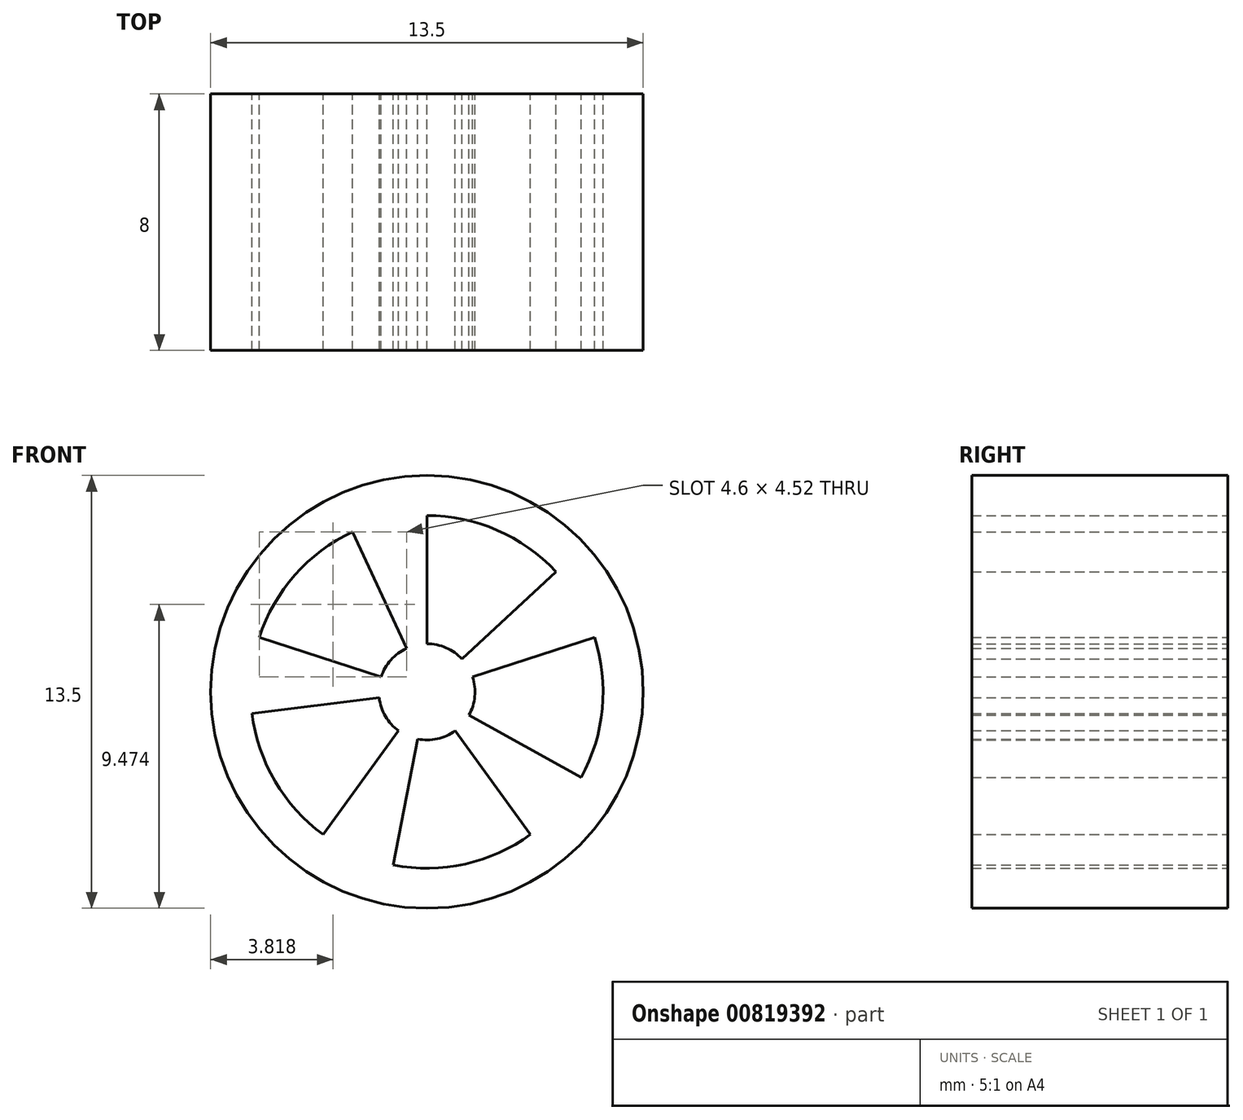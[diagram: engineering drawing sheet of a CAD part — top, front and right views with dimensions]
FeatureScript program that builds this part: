
annotation { "Feature Type Name" : "Feature", "Feature Type Description" : "" }
export const myFeature = defineFeature(function(context is Context, id is Id, definition is map)
    precondition{}
    {
        {
            var Q0;
            Q0=qCreatedBy(makeId("Front.planeOp"),FACE);
            var sketch = newSketch(context, id + "F0", { "sketchPlane" : qUnion([Q0])});
            skCircle(sketch, "E0", {"center": v(0, 0) * mm, "radius": 6.75 * mm});
            skSolve(sketch);
        }
        {
            var Q0;
            Q0=makeQuery(id+"F0.imprint","IMPRINT",FACE,{"disambiguationData":[TD([[makeQuery(id+"F0.imprint","IMPRINT",EDGE,{"derivedFrom":sQuery(id+"F0.wireOp",EDGE,"E0")}),1.0]])]});
            extrude(context, id + "F1", {"entities" : qUnion([Q0]), "depth" : 8 * mm, "offsetDistance" : 25 * mm});
        }
        {
            var Q0;
            Q0=qCreatedBy(makeId("Front.planeOp"),FACE);
            var sketch = newSketch(context, id + "F2", { "sketchPlane" : qUnion([Q0])});
            skCircle(sketch, "E1", {"center": v(0, 0) * mm, "radius": 1.5 * mm});
            skCircle(sketch, "E2", {"center": v(0, 0) * mm, "radius": 5.5 * mm});
            skLineSegment(sketch, "E3", {"start": v(0, 1.5) * mm, "end": v(0, 5.5) * mm});
            skLineSegment(sketch, "E4", {"start": v(-0.63, 1.36) * mm, "end": v(-2.32, 4.98) * mm});
            skPoint(sketch, "E5.orphan", {"position": v(0, 0.27) * mm});
            skLineSegment(sketch, "E6.1.0", {"start": v(-1.43, 0.46) * mm, "end": v(-5.23, 1.7) * mm});
            skLineSegment(sketch, "E6.1.1", {"start": v(-1.49, -0.18) * mm, "end": v(-5.46, -0.67) * mm});
            skLineSegment(sketch, "E6.2.0", {"start": v(-0.88, -1.21) * mm, "end": v(-3.23, -4.45) * mm});
            skLineSegment(sketch, "E6.2.1", {"start": v(-0.29, -1.47) * mm, "end": v(-1.05, -5.4) * mm});
            skLineSegment(sketch, "E6.3.0", {"start": v(0.88, -1.21) * mm, "end": v(3.23, -4.45) * mm});
            skLineSegment(sketch, "E6.3.1", {"start": v(1.31, -0.73) * mm, "end": v(4.81, -2.67) * mm});
            skLineSegment(sketch, "E6.4.0", {"start": v(1.43, 0.46) * mm, "end": v(5.23, 1.7) * mm});
            skLineSegment(sketch, "E6.4.1", {"start": v(1.1, 1.02) * mm, "end": v(4.02, 3.75) * mm});
            skSolve(sketch);
        }
        {
            var Q0;
            {var subQ0=sQuery(id+"F2.wireOp",EDGE,"E6.3.1");Q0=makeQuery(id+"F2.imprint","IMPRINT",FACE,{"disambiguationData":[TD([[makeQuery(id+"F2.imprint","IMPRINT",EDGE,{"derivedFrom":subQ0}),1.0]])]});}
            var Q1;
            {var subQ0=sQuery(id+"F2.wireOp",EDGE,"E3");Q1=makeQuery(id+"F2.imprint","IMPRINT",FACE,{"disambiguationData":[TD([[makeQuery(id+"F2.imprint","IMPRINT",EDGE,{"derivedFrom":subQ0}),-1.0]])]});}
            var Q2;
            {var subQ0=sQuery(id+"F2.wireOp",EDGE,"E4");Q2=makeQuery(id+"F2.imprint","IMPRINT",FACE,{"disambiguationData":[TD([[makeQuery(id+"F2.imprint","IMPRINT",EDGE,{"derivedFrom":subQ0}),1.0]])]});}
            var Q3;
            {var subQ0=sQuery(id+"F2.wireOp",EDGE,"E6.2.1");Q3=makeQuery(id+"F2.imprint","IMPRINT",FACE,{"disambiguationData":[TD([[makeQuery(id+"F2.imprint","IMPRINT",EDGE,{"derivedFrom":subQ0}),1.0]])]});}
            var Q4;
            {var subQ0=sQuery(id+"F2.wireOp",EDGE,"E6.1.1");Q4=makeQuery(id+"F2.imprint","IMPRINT",FACE,{"disambiguationData":[TD([[makeQuery(id+"F2.imprint","IMPRINT",EDGE,{"derivedFrom":subQ0}),1.0]])]});}
            extrude(context, id + "F3", {"entities" : qUnion([Q0, Q1, Q2, Q3, Q4]), "operationType" : NewBodyOperationType.REMOVE, "oppositeDirection" : true, "depth" : -8 * mm, "offsetDistance" : 25 * mm});
        }
    });
